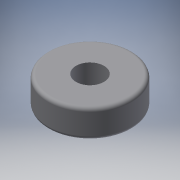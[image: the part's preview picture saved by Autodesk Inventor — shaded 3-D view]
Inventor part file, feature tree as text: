
AUTODESK INVENTOR PART (.ipt)
format: ipt  version: 2016 (Build 200138000, 138)  size: 117,760 bytes
history: native  units: mm
features: extrude x1, fillet x1, sketch x1
ambient origin geometry x8: Origin, YZ Plane, XZ Plane, XY Plane, X Axis, Y Axis, Z Axis, Center Point
bodies: Solid1 (feature_tree)
feature tree (3):
  extrude  "Extrusion1"  Depth=8.0mm
  fillet  "Fillet1"  Radius=8.0mm
  sketch  "Sketch1"  dims[d0=24.0mm d1=8.0mm d2=8.0mm d3=0.0mm d4=1.0mm]
